# Revit family: TIDY T
name_source: partatom
category: Осветительные приборы
revit_build: Autodesk Revit 2016 (Build: 20161004_0715(x64)
units: mm (PartAtom-declared; Revit-internal decimal feet)

## family parameters
Источник света = Нет
Общий = Нет
Основа = Грань
При загрузке вырезать с полостями = Нет
Размер круглого соединителя = Использовать диаметр
Тип детали = Нормальный
Точка расчета площади = Нет

## types (1)
- TIDY T
    ADSK_Единица измерения = Шт.
    ADSK_Завод-изготовитель = ООО МГК Световые технологии
    ADSK_Классификация нагрузок = Прочее
    ADSK_Код изделия = 1444000110
    ADSK_Количество фаз = 1
    ADSK_Количество фаз числовое = 1
    ADSK_Коэффициент мощности = 0.9
    ADSK_Масса = 0.5
    ADSK_Наименование = Трековый светодиодный светильник направленного света. Корпус изготовлен из пластика. Стандартный цвет: WH – белый. В качестве оптического элемента используется линза, стандартный угол – 45°. Возможны специальные модификации для освещения в супермаркетах со специализированными светодиодами. Более подробная информация доступна на сайте
    ADSK_Напряжение = 230 В
    ADSK_Номинальная мощность = 0 кВт
    ADSK_Полная мощность = 0 кВ·А
    ADSK_Размер_Высота = 151 мм
    ADSK_Размер_Радиус = 20 мм
    ADSK_Размер_Ширина = 90 мм
    ADSK_Ток = 0 А
    ADSK_Энергоэффективность = 62 лм/Вт
    IP Class = IP20
    URL = https://ltcompany.com
    Блок аварийного питания = Нет
    Выбор ИС = IES TIDY T : TIDY T 06 WH D45 3000K
    Группа модели = Светильники
    Да = Нет
    Изготовитель = ООО МГК Световые технологии
    Класс Защиты = I
    Климатическая зона = УХЛ4
    Код по классификатору = D5020200
    Корпус = Белый металл
    Корпус X = 70 мм
    Корпус Y = 14 мм
    Нет = Нет
    Область использования = HoReCa/гостиницы/рестораны/кафе, Конференц-залы, Культурно-развлекательные, учреждения, Магазины/бутики, Офисно-административные объекты, ТРЦ, Частные интерьеры
    Описание = Трековый светодиодный светильник направленного света. Корпус изготовлен из пластика. Стандартный цвет: WH – белый. В качестве оптического элемента используется линза, стандартный угол – 45°. Возможны специальные модификации для освещения в супермаркетах со специализированными светодиодами. Более подробная информация доступна на сайте
    Отметка по умолчанию = 0 мм
    Плафон = Плафон самосвечение
    Полная установленная мощность = 0 кВ·А
    Смещение ИС = 21 мм
    Тип ИС = LED
    Тип ПРА = Драйвер
    Тип продукции = Светильник
    Толщина основания = 100 мм

## geometry (parser evidence)
native form markers: Blend x14
no freeform markers — native parametric forms only
